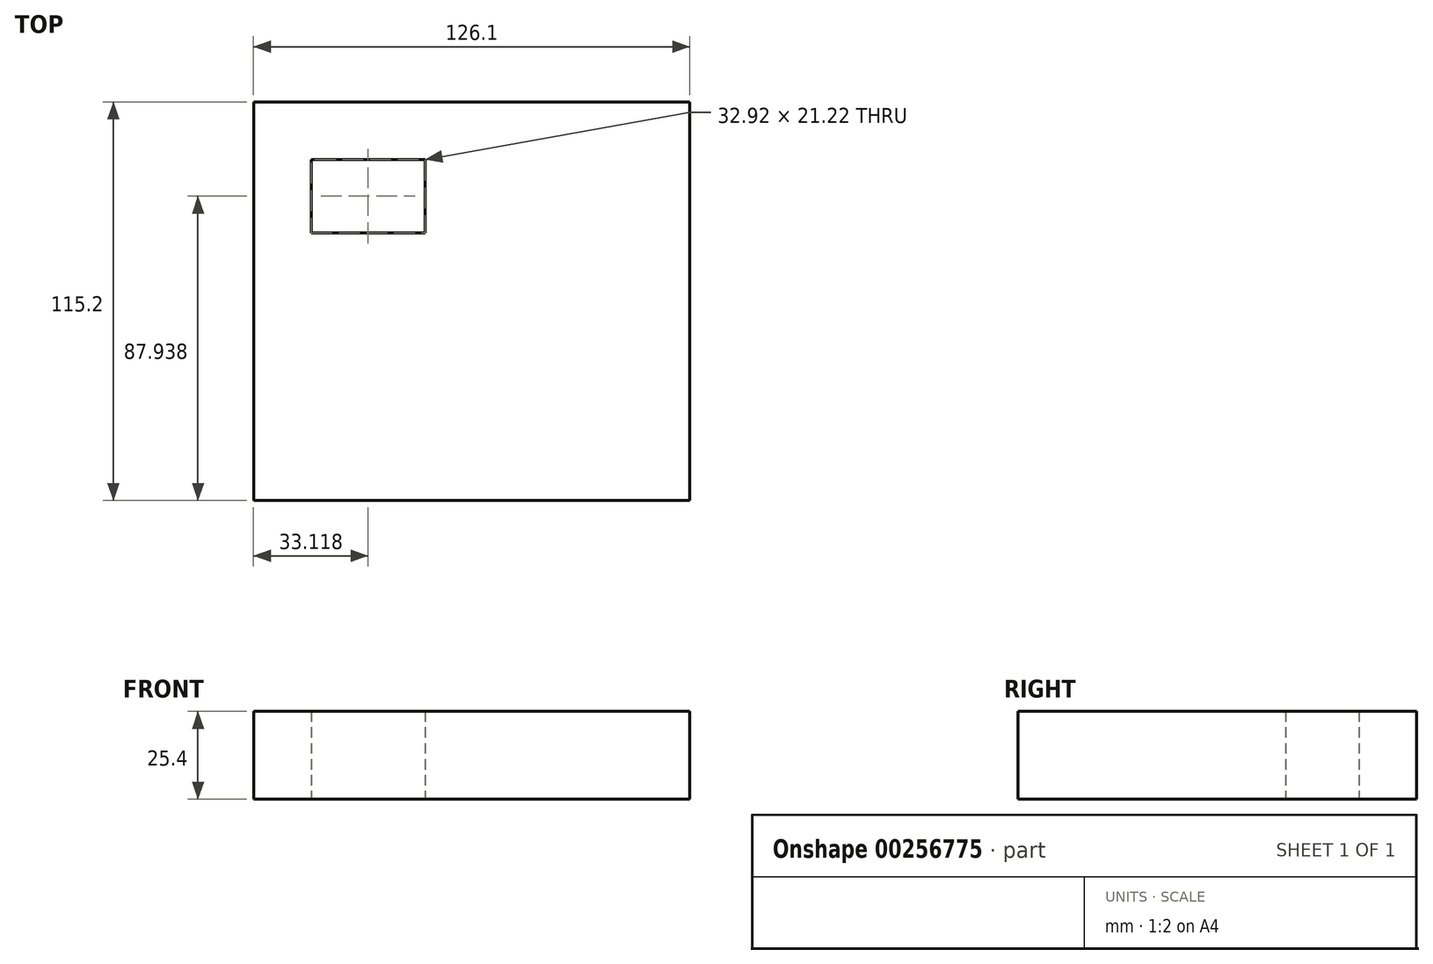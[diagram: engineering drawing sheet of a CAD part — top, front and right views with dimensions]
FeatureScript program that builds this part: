
annotation { "Feature Type Name" : "Feature", "Feature Type Description" : "" }
export const myFeature = defineFeature(function(context is Context, id is Id, definition is map)
    precondition{}
    {
        {
            var Q0;
            Q0=qCreatedBy(makeId("Top.planeOp"),FACE);
            var sketch = newSketch(context, id + "F0", { "sketchPlane" : qUnion([Q0])});
            skLineSegment(sketch, "E0.bottom", {"start": v(-63.05, 57.6) * mm, "end": v(63.05, 57.6) * mm});
            skLineSegment(sketch, "E0.top", {"start": v(-63.05, -57.6) * mm, "end": v(63.05, -57.6) * mm});
            skLineSegment(sketch, "E0.left", {"start": v(-63.05, 57.6) * mm, "end": v(-63.05, -57.6) * mm});
            skLineSegment(sketch, "E0.right", {"start": v(63.05, 57.6) * mm, "end": v(63.05, -57.6) * mm});
            skPoint(sketch, "E0.middle", {"position": v(0, 0) * mm});
            skSolve(sketch);
        }
        {
            var Q0;
            Q0=qCreatedBy(makeId("Top.planeOp"),FACE);
            var sketch = newSketch(context, id + "F1", { "sketchPlane" : qUnion([Q0])});
            skLineSegment(sketch, "E1.bottom", {"start": v(-36.7, 19.35) * mm, "end": v(36.7, 19.35) * mm});
            skLineSegment(sketch, "E1.top", {"start": v(-36.7, -19.35) * mm, "end": v(36.7, -19.35) * mm});
            skLineSegment(sketch, "E1.left", {"start": v(-36.7, 19.35) * mm, "end": v(-36.7, -19.35) * mm});
            skLineSegment(sketch, "E1.right", {"start": v(36.7, 19.35) * mm, "end": v(36.7, -19.35) * mm});
            skPoint(sketch, "E1.middle", {"position": v(0, 0) * mm});
            skSolve(sketch);
        }
        {
            var Q0;
            Q0 = qSketchRegion(id + "F1", true);
            extrude(context, id + "F2", {"entities" : qUnion([Q0]), "depth" : 25.4 * mm});
        }
        {
            var Q0;
            Q0 = qSketchRegion(id + "F0", true);
            extrude(context, id + "F3", {"entities" : qUnion([Q0]), "operationType" : NewBodyOperationType.ADD, "depth" : 25.4 * mm});
        }
        {
            var Q0;
            Q0=qCreatedBy(makeId("Top.planeOp"),FACE);
            var sketch = newSketch(context, id + "F4", { "sketchPlane" : qUnion([Q0])});
            skLineSegment(sketch, "E2.bottom", {"start": v(-46.39, 40.95) * mm, "end": v(-13.47, 40.95) * mm});
            skLineSegment(sketch, "E2.top", {"start": v(-46.39, 19.73) * mm, "end": v(-13.47, 19.73) * mm});
            skLineSegment(sketch, "E2.left", {"start": v(-46.39, 40.95) * mm, "end": v(-46.39, 19.73) * mm});
            skLineSegment(sketch, "E2.right", {"start": v(-13.47, 40.95) * mm, "end": v(-13.47, 19.73) * mm});
            skSolve(sketch);
        }
        {
            var Q0;
            Q0 = qSketchRegion(id + "F4", true);
            extrude(context, id + "F5", {"entities" : qUnion([Q0]), "operationType" : NewBodyOperationType.REMOVE, "depth" : 25.4 * mm});
        }
    });
